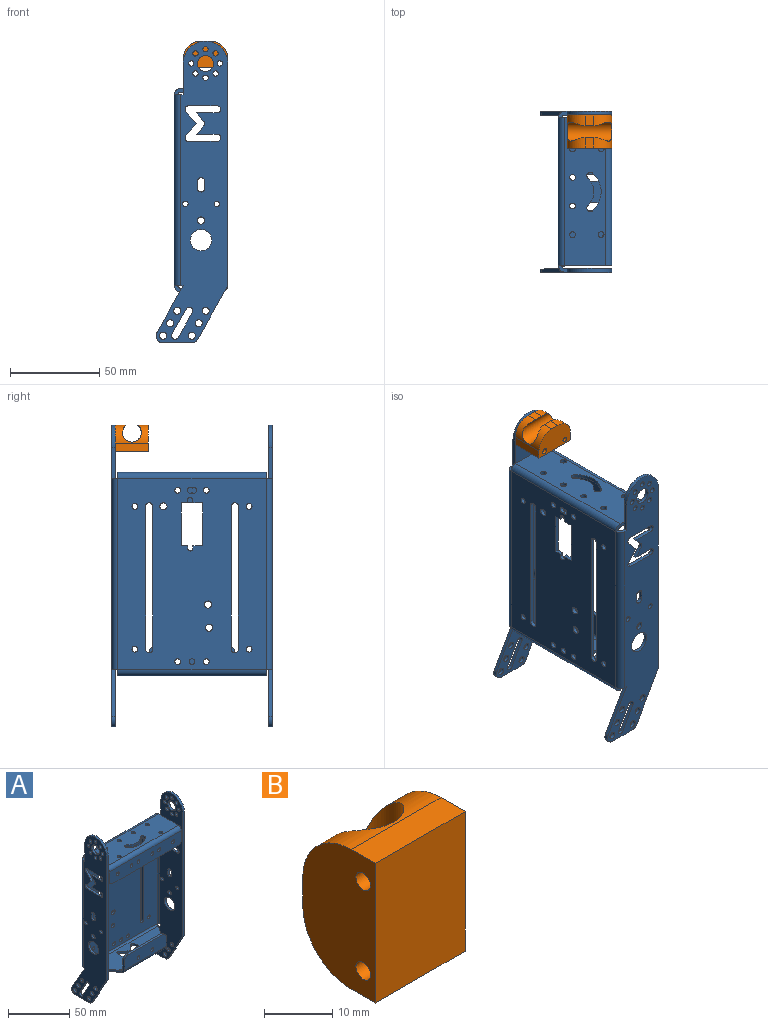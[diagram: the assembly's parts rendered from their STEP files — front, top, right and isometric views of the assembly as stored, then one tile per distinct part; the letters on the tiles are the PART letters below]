
ASSEMBLY  parts=2 mates=1
PART A: 209 faces, bbox 90x40.2x169 mm
  f0: cylinder r=4mm len=4mm, axis (0,-1,0), area 12.6mm2, adj f1,f2,f17,f20
  f1: plane 48x13.5mm, normal (0,1,0), area 624.6mm2, adj f0,f2,f16,f17,f34,f64,f67,f106
  f2: plane 40x2mm, normal (0,0,1), area 80mm2, adj f0,f1,f16,f20
  f3: cylinder r=4mm len=4mm, axis (0,-1,0), area 12.6mm2, adj f4,f5,f184,f185
  f4: plane 75x2mm, normal (0,0,-1), area 150mm2, adj f3,f5,f14,f185
  f5: plane 83x13.5mm, normal (0,1,0), area 1064.2mm2, adj f3,f4,f14,f15,f35,f36,f37,f107
  f6: cylinder r=4mm len=3.49mm, axis (1,0,0), area 8.5mm2, adj f7,f8,f61,f199
  f7: plane 15.82x2mm, normal (0,0,-1), area 31.6mm2, adj f6,f8,f9,f199
  f8: plane 169x40.16mm, normal (-1,0,0), area 3649.8mm2, adj f6,f7,f9,f41,f42,f43,f44,f45
  f9: cylinder r=4mm len=5.96mm, axis (1,0,0), area 16.7mm2, adj f7,f8,f60,f199
  f10: cylinder r=4mm len=5.96mm, axis (-1,0,0), area 16.7mm2, adj f11,f12,f178,f203
  f11: plane 15.82x2mm, normal (0,0,-1), area 31.6mm2, adj f10,f12,f13,f203
  f12: plane 169x40.16mm, normal (1,0,0), area 3649.8mm2, adj f10,f11,f13,f117,f119,f120,f122,f123
  f13: cylinder r=4mm len=3.49mm, axis (-1,0,0), area 8.5mm2, adj f11,f12,f179,f203
  f14: cylinder r=4mm len=4mm, axis (0,-1,0), area 12.6mm2, adj f4,f5,f15,f185
  f15: plane 30x13mm, normal (1,0,0), area 80.7mm2, adj f5,f14,f182,f183,f185,f186,f193,f194
  f16: cylinder r=4mm len=4mm, axis (0,1,0), area 12.6mm2, adj f1,f2,f20,f64
  f17: plane 13x4.5mm, normal (-1,0,0), area 28.9mm2, adj f0,f1,f19,f20,f21,f22,f67,f68
  f18: plane 2x1mm, normal (1,0,0), area 2mm2, adj f19,f22,f68,f187
  f19: cylinder r=0.5mm len=2mm, axis (0,0,-1), area 3.1mm2, adj f17,f18,f22,f68
  f20: plane 48x13.5mm, normal (0,-1,0), area 624.6mm2, adj f0,f2,f16,f17,f21,f34,f64,f106
  f21: cylinder r=3.5mm len=48mm, axis (-1,0,0), area 263.9mm2, adj f17,f20,f22,f64
  f22: plane 83x23mm, normal (0,0,-1), area 1310.2mm2, adj f17,f18,f19,f21,f64,f65,f66,f69
  f23: cylinder r=1.62mm len=3.24mm, axis (0,-1,0), area 14.5mm2, adj f28,f29,f204
  f24: cylinder r=1.62mm len=3.24mm, axis (0,-1,0), area 20.4mm2, adj f29,f204
  f25: cylinder r=1.62mm len=3.24mm, axis (0,-1,0), area 20.4mm2, adj f29,f204
  f26: cylinder r=1.62mm len=3.24mm, axis (0,-1,0), area 20.4mm2, adj f29,f204
  f27: cylinder r=1.62mm len=3.24mm, axis (0,-1,0), area 20.4mm2, adj f29,f204
  f28: cylinder r=1.62mm len=3.24mm, axis (0,1,0), area 14.5mm2, adj f23,f29,f204
  f29: plane 107x83mm, normal (0,-1,0), area 7785.6mm2, adj f23,f24,f25,f26,f27,f28,f30,f31
  f30: cylinder r=2mm len=4mm, axis (0,1,0), area 12.6mm2, adj f29,f31,f33,f204
  f31: plane 80x2mm, normal (-1,0,0), area 160mm2, adj f29,f30,f32,f204
  f32: cylinder r=2mm len=4mm, axis (0,1,0), area 12.6mm2, adj f29,f31,f33,f204
  f33: plane 80x2mm, normal (1,0,0), area 160mm2, adj f29,f30,f32,f204
  f34: cylinder r=1.62mm len=3.24mm, axis (0,1,0), area 20.4mm2, adj f1,f20
  f35: cylinder r=1.62mm len=3.24mm, axis (0,1,0), area 20.4mm2, adj f5,f185
  f36: cylinder r=1.62mm len=3.24mm, axis (0,1,0), area 20.4mm2, adj f5,f185
  f37: cylinder r=1.62mm len=3.24mm, axis (0,1,0), area 20.4mm2, adj f5,f185
  f38: cylinder r=1.62mm len=3.24mm, axis (0,0,-1), area 20.4mm2, adj f194,f195
  f39: cylinder r=1.62mm len=3.24mm, axis (0,0,-1), area 20.4mm2, adj f194,f195
  f40: cylinder r=1.62mm len=3.24mm, axis (0,0,-1), area 20.4mm2, adj f194,f195
  f41: cylinder r=2mm len=3.74mm, axis (-1,0,0), area 12.6mm2, adj f8,f42,f44,f199
  f42: plane 13.95x7.84mm, normal (0,-0.87,-0.49), area 32mm2, adj f8,f41,f43,f199
  f43: cylinder r=2mm len=3.74mm, axis (-1,0,0), area 12.6mm2, adj f8,f42,f44,f199
  f44: plane 13.95x7.84mm, normal (0,0.87,0.49), area 32mm2, adj f8,f41,f43,f199
  f45: cylinder r=1.5mm len=3mm, axis (1,0,0), area 18.8mm2, adj f8,f199
  f46: cylinder r=1.5mm len=3mm, axis (1,0,0), area 18.8mm2, adj f8,f199
  f47: cylinder r=1.5mm len=3mm, axis (1,0,0), area 18.8mm2, adj f8,f199
  f48: cylinder r=1.5mm len=3mm, axis (1,0,0), area 18.8mm2, adj f8,f199
  f49: cylinder r=1.5mm len=3mm, axis (1,0,0), area 18.8mm2, adj f8,f199
  f50: cylinder r=1.5mm len=3mm, axis (1,0,0), area 18.8mm2, adj f8,f199
  f51: cylinder r=1.5mm len=3mm, axis (1,0,0), area 18.8mm2, adj f8,f199
  f52: cylinder r=1.5mm len=3mm, axis (1,0,0), area 18.8mm2, adj f8,f199
  f53: cylinder r=2mm len=4mm, axis (1,0,0), area 25.1mm2, adj f8,f199
  f54: cylinder r=2mm len=4mm, axis (1,0,0), area 25.1mm2, adj f8,f199
  f55: cylinder r=2mm len=4mm, axis (1,0,0), area 25.1mm2, adj f8,f199
  f56: cylinder r=2mm len=4mm, axis (1,0,0), area 25.1mm2, adj f8,f199
  f57: cylinder r=2mm len=4mm, axis (1,0,0), area 25.1mm2, adj f8,f199
  f58: cylinder r=2mm len=4mm, axis (1,0,0), area 25.1mm2, adj f8,f199
  f59: cylinder r=4.5mm len=9mm, axis (1,0,0), area 56.5mm2, adj f8,f199
  f60: plane 26.04x14.65mm, normal (0,0.87,0.49), area 59.8mm2, adj f8,f9,f197,f199
  f61: plane 29.96x16.85mm, normal (0,-0.87,-0.49), area 68.8mm2, adj f6,f8,f199,f207
  f62: plane 17.5x2mm, normal (0,1,0), area 35mm2, adj f8,f63,f199,f200
  f63: cylinder r=12.5mm len=25mm, axis (-1,0,0), area 78.5mm2, adj f8,f62,f199,f207
  f64: plane 13x4.5mm, normal (1,0,0), area 28.9mm2, adj f1,f16,f20,f21,f22,f65,f67,f68
  f65: cylinder r=0.5mm len=2mm, axis (0,0,1), area 3.1mm2, adj f22,f64,f66,f68
  f66: plane 2x1mm, normal (-1,0,0), area 2mm2, adj f22,f65,f68,f188
  f67: cylinder r=1.5mm len=48mm, axis (-1,0,0), area 113.1mm2, adj f1,f17,f64,f68
  f68: plane 83x23mm, normal (0,0,1), area 1310.2mm2, adj f17,f18,f19,f64,f65,f66,f67,f69
  f69: plane 4.68x4.1mm, normal (-0.66,0.75,0), area 12.4mm2, adj f22,f68,f70,f81
  f70: cylinder r=2mm len=2.63mm, axis (0,0,1), area 5.8mm2, adj f22,f68,f69,f71
  f71: plane 4.68x4.1mm, normal (0.66,0.75,0), area 12.4mm2, adj f22,f68,f70,f72
  f72: plane 11.59x2mm, normal (-1,0,0), area 23.2mm2, adj f22,f68,f71,f73
  f73: cylinder r=2mm len=4mm, axis (0,0,1), area 12.6mm2, adj f22,f68,f72,f74
  f74: plane 16x2mm, normal (1,0,0), area 32mm2, adj f22,f68,f73,f75
  f75: cylinder r=2mm len=3.32mm, axis (0,0,1), area 9.2mm2, adj f22,f68,f74,f76
  f76: plane 6.68x5.85mm, normal (-0.66,-0.75,0), area 17.8mm2, adj f22,f68,f75,f77
  f77: plane 6.68x5.85mm, normal (0.66,-0.75,0), area 17.8mm2, adj f22,f68,f76,f78
  f78: cylinder r=2mm len=3.32mm, axis (0,0,1), area 9.2mm2, adj f22,f68,f77,f79
  f79: plane 16x2mm, normal (-1,0,0), area 32mm2, adj f22,f68,f78,f80
  f80: cylinder r=2mm len=4mm, axis (0,0,1), area 12.6mm2, adj f22,f68,f79,f81
  f81: plane 11.59x2mm, normal (1,0,0), area 23.2mm2, adj f22,f68,f69,f80
  f82: cylinder r=2mm len=4mm, axis (0,1,0), area 25.1mm2, adj f29,f204
  f83: cylinder r=2mm len=4mm, axis (0,1,0), area 25.1mm2, adj f29,f204
  f84: cylinder r=2mm len=4mm, axis (0,1,0), area 25.1mm2, adj f29,f204
  f85: cylinder r=1.62mm len=3.24mm, axis (0,1,0), area 20.4mm2, adj f29,f204
  f86: cylinder r=1.62mm len=3.24mm, axis (0,1,0), area 20.4mm2, adj f29,f204
  f87: cylinder r=1.62mm len=3.24mm, axis (0,1,0), area 20.4mm2, adj f29,f204
  f88: cylinder r=1.62mm len=3.24mm, axis (0,1,0), area 20.4mm2, adj f29,f204
  f89: cylinder r=1.62mm len=3.24mm, axis (0,1,0), area 20.4mm2, adj f29,f204
  f90: plane 5.5x2mm, normal (0,0,-1), area 11mm2, adj f29,f91,f101,f204
  f91: plane 2x1.5mm, normal (1,0,0), area 3mm2, adj f29,f90,f92,f204
  f92: cylinder r=1.5mm len=3mm, axis (0,-1,0), area 9.4mm2, adj f29,f91,f93,f204
  f93: plane 2x1.5mm, normal (-1,0,0), area 3mm2, adj f29,f92,f94,f204
  f94: plane 3.5x2mm, normal (0,0,-1), area 7mm2, adj f29,f93,f95,f204
  f95: plane 24x2mm, normal (-1,0,0), area 48mm2, adj f29,f94,f96,f204
  f96: plane 3.5x2mm, normal (0,0,1), area 7mm2, adj f29,f95,f97,f204
  f97: plane 2x1.5mm, normal (-1,0,0), area 3mm2, adj f29,f96,f98,f204
  f98: cylinder r=1.5mm len=3mm, axis (0,-1,0), area 9.4mm2, adj f29,f97,f99,f204
  f99: plane 2x1.5mm, normal (1,0,0), area 3mm2, adj f29,f98,f100,f204
  f100: plane 5.5x2mm, normal (0,0,1), area 11mm2, adj f29,f99,f101,f204
  f101: plane 24x2mm, normal (1,0,0), area 48mm2, adj f29,f90,f100,f204
  f102: cylinder r=2mm len=4mm, axis (0,-1,0), area 12.6mm2, adj f29,f103,f105,f204
  f103: plane 80x2mm, normal (1,0,0), area 160mm2, adj f29,f102,f104,f204
  f104: cylinder r=2mm len=4mm, axis (0,-1,0), area 12.6mm2, adj f29,f103,f105,f204
  f105: plane 80x2mm, normal (-1,0,0), area 160mm2, adj f29,f102,f104,f204
  f106: cylinder r=1.62mm len=3.24mm, axis (0,-1,0), area 20.4mm2, adj f1,f20
  f107: cylinder r=1.62mm len=3.24mm, axis (0,-1,0), area 20.4mm2, adj f5,f185
  f108: cylinder r=1.62mm len=3.24mm, axis (0,-1,0), area 20.4mm2, adj f5,f185
  f109: cylinder r=1.62mm len=3.24mm, axis (0,-1,0), area 20.4mm2, adj f5,f185
  f110: cylinder r=1.62mm len=3.24mm, axis (0,0,1), area 20.4mm2, adj f194,f195
  f111: cylinder r=1.62mm len=3.24mm, axis (0,0,1), area 20.4mm2, adj f194,f195
  f112: cylinder r=1.62mm len=3.24mm, axis (0,0,1), area 20.4mm2, adj f194,f195
  f113: cylinder r=2mm len=3.48mm, axis (0,0,-1), area 12.6mm2, adj f114,f116,f194,f195
  f114: cylinder r=10.12mm len=15.03mm, axis (0,0,-1), area 33.9mm2, adj f113,f115,f194,f195
  f115: cylinder r=2mm len=3.48mm, axis (0,0,-1), area 12.6mm2, adj f114,f116,f194,f195
  f116: cylinder r=14.12mm len=20.97mm, axis (0,0,-1), area 47.3mm2, adj f113,f115,f194,f195
  f117: cylinder r=2mm len=3.32mm, axis (-1,0,0), area 9.2mm2, adj f12,f119,f120,f203
  f118: cylinder r=2mm len=3.32mm, axis (-1,0,0), area 9.2mm2, adj f8,f121,f137,f199
  f119: plane 6.68x5.85mm, normal (0,-0.75,-0.66), area 17.8mm2, adj f12,f117,f122,f203
  f120: plane 16x2mm, normal (0,0,1), area 32mm2, adj f12,f117,f123,f203
  f121: plane 16x2mm, normal (0,0,1), area 32mm2, adj f8,f118,f124,f199
  f122: plane 6.68x5.85mm, normal (0,-0.75,0.66), area 17.8mm2, adj f12,f119,f125,f203
  f123: cylinder r=2mm len=4mm, axis (-1,0,0), area 12.6mm2, adj f12,f120,f126,f203
  f124: cylinder r=2mm len=4mm, axis (-1,0,0), area 12.6mm2, adj f8,f121,f127,f199
  f125: cylinder r=2mm len=3.32mm, axis (-1,0,0), area 9.2mm2, adj f12,f122,f128,f203
  f126: plane 11.59x2mm, normal (0,0,-1), area 23.2mm2, adj f12,f123,f129,f203
  f127: plane 11.59x2mm, normal (0,0,-1), area 23.2mm2, adj f8,f124,f130,f199
  f128: plane 16x2mm, normal (0,0,-1), area 32mm2, adj f12,f125,f131,f203
  f129: plane 4.68x4.1mm, normal (0,0.75,0.66), area 12.4mm2, adj f12,f126,f132,f203
  f130: plane 4.68x4.1mm, normal (0,0.75,0.66), area 12.4mm2, adj f8,f127,f133,f199
  f131: cylinder r=2mm len=4mm, axis (-1,0,0), area 12.6mm2, adj f12,f128,f134,f203
  f132: cylinder r=2mm len=2.63mm, axis (-1,0,0), area 5.8mm2, adj f12,f129,f135,f203
  f133: cylinder r=2mm len=2.63mm, axis (-1,0,0), area 5.8mm2, adj f8,f130,f136,f199
  f134: plane 11.59x2mm, normal (0,0,1), area 23.2mm2, adj f12,f131,f135,f203
  f135: plane 4.68x4.1mm, normal (0,0.75,-0.66), area 12.4mm2, adj f12,f132,f134,f203
  f136: plane 4.68x4.1mm, normal (0,0.75,-0.66), area 12.4mm2, adj f8,f133,f142,f199
  f137: plane 6.68x5.85mm, normal (0,-0.75,-0.66), area 17.8mm2, adj f8,f118,f138,f199
  f138: plane 6.68x5.85mm, normal (0,-0.75,0.66), area 17.8mm2, adj f8,f137,f139,f199
  f139: cylinder r=2mm len=3.32mm, axis (-1,0,0), area 9.2mm2, adj f8,f138,f140,f199
  f140: plane 16x2mm, normal (0,0,-1), area 32mm2, adj f8,f139,f141,f199
  f141: cylinder r=2mm len=4mm, axis (-1,0,0), area 12.6mm2, adj f8,f140,f142,f199
  f142: plane 11.59x2mm, normal (0,0,1), area 23.2mm2, adj f8,f136,f141,f199
  f143: cylinder r=2mm len=4mm, axis (-1,0,0), area 12.6mm2, adj f12,f145,f147,f203
  f144: cylinder r=2mm len=4mm, axis (-1,0,0), area 12.6mm2, adj f8,f146,f150,f199
  f145: plane 4x2mm, normal (0,-1,0), area 8mm2, adj f12,f143,f148,f203
  f146: plane 4x2mm, normal (0,-1,0), area 8mm2, adj f8,f144,f149,f199
  f147: plane 4x2mm, normal (0,1,0), area 8mm2, adj f12,f143,f148,f203
  f148: cylinder r=2mm len=4mm, axis (-1,0,0), area 12.6mm2, adj f12,f145,f147,f203
  f149: cylinder r=2mm len=4mm, axis (-1,0,0), area 12.6mm2, adj f8,f146,f150,f199
  f150: plane 4x2mm, normal (0,1,0), area 8mm2, adj f8,f144,f149,f199
  f151: cylinder r=1.5mm len=3mm, axis (1,0,0), area 18.8mm2, adj f12,f203
  f152: cylinder r=1.5mm len=3mm, axis (1,0,0), area 18.8mm2, adj f8,f199
  f153: cylinder r=1.5mm len=3mm, axis (1,0,0), area 18.8mm2, adj f12,f203
  f154: cylinder r=1.5mm len=3mm, axis (1,0,0), area 18.8mm2, adj f8,f199
  f155: cylinder r=6mm len=12mm, axis (1,0,0), area 75.4mm2, adj f12,f203
  f156: cylinder r=6mm len=12mm, axis (1,0,0), area 75.4mm2, adj f8,f199
  f157: cylinder r=2mm len=3.74mm, axis (-1,0,0), area 12.6mm2, adj f12,f158,f160,f203
  f158: plane 13.95x7.84mm, normal (0,-0.87,-0.49), area 32mm2, adj f12,f157,f159,f203
  f159: cylinder r=2mm len=3.74mm, axis (-1,0,0), area 12.6mm2, adj f12,f158,f160,f203
  f160: plane 13.95x7.84mm, normal (0,0.87,0.49), area 32mm2, adj f12,f157,f159,f203
  f161: cylinder r=1.5mm len=3mm, axis (1,0,0), area 18.8mm2, adj f12,f203
  f162: cylinder r=1.5mm len=3mm, axis (1,0,0), area 18.8mm2, adj f12,f203
  f163: cylinder r=1.5mm len=3mm, axis (1,0,0), area 18.8mm2, adj f12,f203
  f164: cylinder r=1.5mm len=3mm, axis (1,0,0), area 18.8mm2, adj f12,f203
  f165: cylinder r=1.5mm len=3mm, axis (1,0,0), area 18.8mm2, adj f12,f203
  f166: cylinder r=1.5mm len=3mm, axis (1,0,0), area 18.8mm2, adj f12,f203
  f167: cylinder r=1.5mm len=3mm, axis (1,0,0), area 18.8mm2, adj f12,f203
  f168: cylinder r=1.5mm len=3mm, axis (1,0,0), area 18.8mm2, adj f12,f203
  f169: cylinder r=2mm len=4mm, axis (1,0,0), area 25.1mm2, adj f12,f203
  f170: cylinder r=2mm len=4mm, axis (1,0,0), area 25.1mm2, adj f12,f203
  f171: cylinder r=2mm len=4mm, axis (1,0,0), area 25.1mm2, adj f12,f203
  f172: cylinder r=2mm len=4mm, axis (1,0,0), area 25.1mm2, adj f12,f203
  f173: cylinder r=2mm len=4mm, axis (1,0,0), area 25.1mm2, adj f12,f203
  f174: cylinder r=2mm len=4mm, axis (1,0,0), area 25.1mm2, adj f12,f203
  f175: cylinder r=2mm len=4mm, axis (1,0,0), area 25.1mm2, adj f12,f203
  f176: cylinder r=2mm len=4mm, axis (1,0,0), area 25.1mm2, adj f8,f199
  f177: cylinder r=4.5mm len=9mm, axis (1,0,0), area 56.5mm2, adj f12,f203
  f178: plane 26.04x14.65mm, normal (0,0.87,0.49), area 59.8mm2, adj f10,f12,f203,f205
  f179: plane 29.96x16.85mm, normal (0,-0.87,-0.49), area 68.8mm2, adj f12,f13,f203,f206
  f180: plane 17.5x2mm, normal (0,1,0), area 35mm2, adj f12,f181,f182,f203
  f181: cylinder r=12.5mm len=25mm, axis (-1,0,0), area 78.5mm2, adj f12,f180,f203,f206
  f182: plane 5x3.5mm, normal (0,0,1), area 10.9mm2, adj f12,f15,f180,f201,f203,f208
  f183: cylinder r=3.5mm len=83mm, axis (1,0,0), area 456.3mm2, adj f15,f184,f185,f195
  f184: plane 30x13mm, normal (-1,0,0), area 80.7mm2, adj f3,f5,f183,f185,f186,f193,f194,f195
  f185: plane 83x13.5mm, normal (0,-1,0), area 1064.2mm2, adj f3,f4,f14,f15,f35,f36,f37,f107
  f186: cylinder r=1.5mm len=83mm, axis (1,0,0), area 195.6mm2, adj f5,f15,f184,f194
  f187: plane 23x16.5mm, normal (-0.81,-0.58,0), area 56.6mm2, adj f18,f22,f68,f190
  f188: plane 23x16.5mm, normal (0.81,-0.58,0), area 56.6mm2, adj f22,f66,f68,f191
  f189: cylinder r=3.5mm len=83mm, axis (-1,0,0), area 456.3mm2, adj f22,f190,f191,f204
  f190: plane 3.5x3.5mm, normal (-1,0,0), area 7.9mm2, adj f187,f189,f192,f197
  f191: plane 3.5x3.5mm, normal (1,0,0), area 7.9mm2, adj f188,f189,f192,f205
  f192: cylinder r=1.5mm len=83mm, axis (-1,0,0), area 195.6mm2, adj f29,f68,f190,f191
  f193: cylinder r=3.5mm len=83mm, axis (1,0,0), area 456.3mm2, adj f15,f184,f195,f204
  f194: plane 83x23mm, normal (0,0,-1), area 1765.8mm2, adj f15,f38,f39,f40,f110,f111,f112,f113
  f195: plane 83x23mm, normal (0,0,1), area 1765.8mm2, adj f15,f38,f39,f40,f110,f111,f112,f113
  f196: cylinder r=1.5mm len=83mm, axis (1,0,0), area 195.6mm2, adj f15,f29,f184,f194
  f197: plane 5x3.5mm, normal (0,0,-1), area 10.9mm2, adj f8,f60,f190,f198,f199,f202
  f198: cylinder r=3.5mm len=107mm, axis (0,0,1), area 588.3mm2, adj f8,f197,f200,f204
  f199: plane 169x40.16mm, normal (1,0,0), area 3649.8mm2, adj f6,f7,f9,f41,f42,f43,f44,f45
  f200: plane 5x3.5mm, normal (0,0,1), area 10.9mm2, adj f8,f62,f184,f198,f199,f202
  f201: cylinder r=3.5mm len=107mm, axis (0,0,1), area 588.3mm2, adj f12,f182,f204,f205
  f202: cylinder r=1.5mm len=107mm, axis (0,0,1), area 252.1mm2, adj f29,f197,f199,f200
  f203: plane 169x40.16mm, normal (-1,0,0), area 3649.8mm2, adj f10,f11,f13,f117,f119,f120,f122,f123
  f204: plane 107x83mm, normal (0,1,0), area 7785.6mm2, adj f23,f24,f25,f26,f27,f28,f30,f31
  f205: plane 5x3.5mm, normal (0,0,-1), area 10.9mm2, adj f12,f178,f191,f201,f203,f208
  f206: plane 124.5x2mm, normal (0,-1,0), area 249mm2, adj f12,f179,f181,f203
  f207: plane 124.5x2mm, normal (0,-1,0), area 249mm2, adj f8,f61,f63,f199
  f208: cylinder r=1.5mm len=107mm, axis (0,0,1), area 252.1mm2, adj f29,f182,f203,f205
PART B: 12 faces, bbox 18.6x15x25 mm
  f0: plane 6x5mm, normal (0,1,0), area 30mm2, adj f1,f5,f10,f11
  f1: plane 25x15mm, normal (-1,0,0), area 317.9mm2, adj f0,f2,f6,f7,f8,f9,f10,f11
  f2: plane 25x18.6mm, normal (0,-1,0), area 465mm2, adj f1,f3,f6,f7
  f3: plane 25x15mm, normal (1,0,0), area 317.9mm2, adj f2,f4,f6,f7,f8,f9,f10,f11
  f4: plane 6x5mm, normal (0,1,0), area 30mm2, adj f3,f5,f10,f11
  f5: cylinder r=5.3mm len=24.97mm, axis (0,0,-1), area 551.8mm2, adj f0,f4,f10,f11
  f6: plane 18.6x5mm, normal (0,0,1), area 93mm2, adj f1,f2,f3,f11
  f7: plane 18.6x5mm, normal (0,0,-1), area 93mm2, adj f1,f2,f3,f10
  f8: cylinder r=1.5mm len=18.6mm, axis (-1,0,0), area 175.3mm2, adj f1,f3
  f9: cylinder r=1.5mm len=18.6mm, axis (-1,0,0), area 175.3mm2, adj f1,f3
  f10: cylinder r=10mm len=18.6mm, axis (-1,0,0), area 162.5mm2, adj f0,f1,f3,f4,f5,f7
  f11: cylinder r=10mm len=18.6mm, axis (1,0,0), area 162.5mm2, adj f0,f1,f3,f4,f5,f6
PLACE A rot(axis=(0,0,1),90deg) t=(-17.85,119.11,114.71)mm
PLACE B rot(axis=(0.58,-0.58,-0.58),120deg) t=(-17.85,143.51,129.71)mm
MATE fastened A.f52 <-> B.f9  axis (0,-1,0) through (-38.35,162.11,132.21)mm
